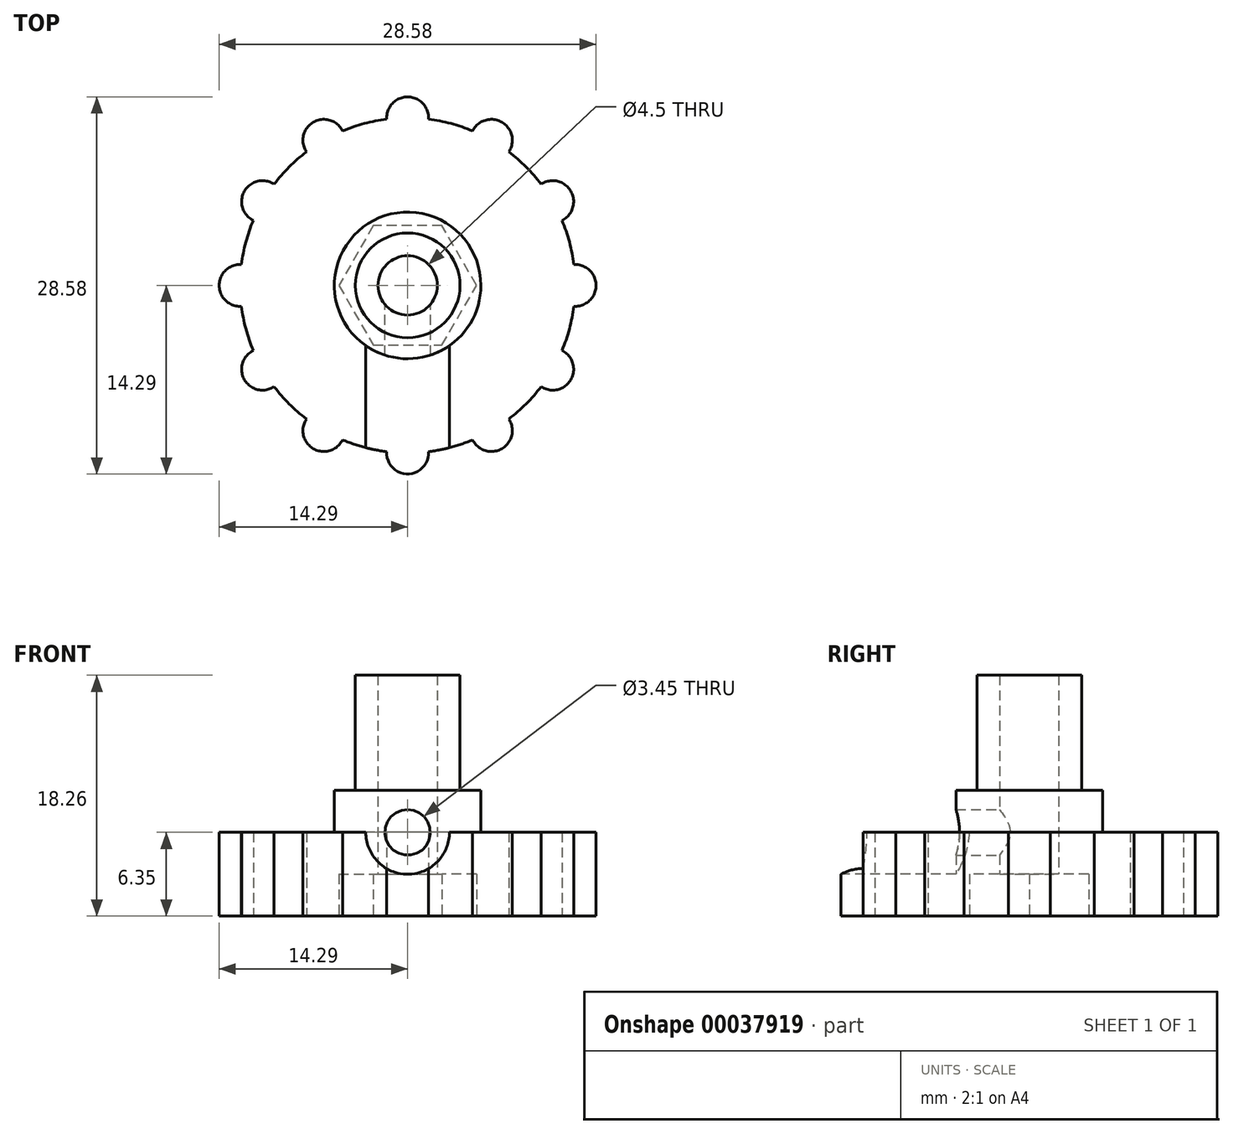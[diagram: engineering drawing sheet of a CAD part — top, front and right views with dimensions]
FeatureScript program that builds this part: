
annotation { "Feature Type Name" : "Feature", "Feature Type Description" : "" }
export const myFeature = defineFeature(function(context is Context, id is Id, definition is map)
    precondition{}
    {
        {
            var Q0;
            Q0=qCreatedBy(makeId("Top.planeOp"),FACE);
            var sketch = newSketch(context, id + "F0", { "sketchPlane" : qUnion([Q0])});
            skCircle(sketch, "E0", {"center": v(0, 0) * mm, "radius": 12.7 * mm});
            skSolve(sketch);
        }
        {
            var Q0;
            Q0 = qSketchRegion(id + "F0", true);
            extrude(context, id + "F1", {"entities" : qUnion([Q0]), "depth" : 6.35 * mm});
        }
        {
            var Q0;
            Q0=makeQuery(id+"F1.opExtrude","CAP_FACE",FACE,{"disambiguationData":[OSD([sQuery(id+"F0.wireOp",EDGE,"E0")])],"isStart":true});
            var sketch = newSketch(context, id + "F2", { "sketchPlane" : qUnion([Q0])});
            skCircle(sketch, "E1.cCircle", {"center": v(0, 0) * mm, "radius": 4.52 * mm, "construction": true});
            skLineSegment(sketch, "E1.0", {"start": v(-2.61, 4.52) * mm, "end": v(2.61, 4.52) * mm});
            skLineSegment(sketch, "E1.1", {"start": v(2.61, 4.52) * mm, "end": v(5.22, 0) * mm});
            skLineSegment(sketch, "E1.2", {"start": v(5.22, 0) * mm, "end": v(2.61, -4.52) * mm});
            skLineSegment(sketch, "E1.3", {"start": v(2.61, -4.52) * mm, "end": v(-2.61, -4.52) * mm});
            skLineSegment(sketch, "E1.4", {"start": v(-2.61, -4.52) * mm, "end": v(-5.22, 0) * mm});
            skLineSegment(sketch, "E1.5", {"start": v(-5.22, 0) * mm, "end": v(-2.61, 4.52) * mm});
            skPoint(sketch, "E1.0.midPoint", {"position": v(0, 4.52) * mm});
            skSolve(sketch);
        }
        {
            var Q0;
            Q0 = qSketchRegion(id + "F2", true);
            extrude(context, id + "F3", {"entities" : qUnion([Q0]), "operationType" : NewBodyOperationType.REMOVE, "oppositeDirection" : true, "depth" : 3.17 * mm});
        }
        {
            var Q0;
            Q0=makeQuery(id+"F1.opExtrude","CAP_FACE",FACE,{"disambiguationData":[OSD([sQuery(id+"F0.wireOp",EDGE,"E0")])],"isStart":false});
            var sketch = newSketch(context, id + "F4", { "sketchPlane" : qUnion([Q0])});
            skCircle(sketch, "E2", {"center": v(0, 0) * mm, "radius": 5.56 * mm});
            skSolve(sketch);
        }
        {
            var Q0;
            Q0 = qSketchRegion(id + "F4", true);
            extrude(context, id + "F5", {"entities" : qUnion([Q0]), "operationType" : NewBodyOperationType.ADD, "depth" : 3.17 * mm});
        }
        {
            var Q0;
            Q0=makeQuery(id+"F5.opExtrude","CAP_FACE",FACE,{"disambiguationData":[OSD([sQuery(id+"F4.wireOp",EDGE,"E2")])],"isStart":false});
            var sketch = newSketch(context, id + "F6", { "sketchPlane" : qUnion([Q0])});
            skCircle(sketch, "E3", {"center": v(0, 0) * mm, "radius": 3.97 * mm});
            skSolve(sketch);
        }
        {
            var Q0;
            Q0 = qSketchRegion(id + "F6", true);
            extrude(context, id + "F7", {"entities" : qUnion([Q0]), "operationType" : NewBodyOperationType.ADD, "depth" : 8.73 * mm});
        }
        {
            var Q0;
            Q0=makeQuery(id+"F3.boolean.opBoolean","COPY",FACE,{"derivedFrom":makeQuery(id+"F3.opExtrude","CAP_FACE",FACE,{"disambiguationData":[OSD([sQuery(id+"F2.wireOp",EDGE,"E1.0"),sQuery(id+"F2.wireOp",EDGE,"E1.1"),sQuery(id+"F2.wireOp",EDGE,"E1.2"),sQuery(id+"F2.wireOp",EDGE,"E1.3"),sQuery(id+"F2.wireOp",EDGE,"E1.4"),sQuery(id+"F2.wireOp",EDGE,"E1.5")])],"isStart":false})});
            var sketch = newSketch(context, id + "F8", { "sketchPlane" : qUnion([Q0])});
            skCircle(sketch, "E4", {"center": v(0, 0) * mm, "radius": 2.25 * mm});
            skSolve(sketch);
        }
        {
            var Q0;
            Q0 = qSketchRegion(id + "F8", true);
            var Q1;
            Q1=makeQuery(id+"F7.opExtrude","CAP_FACE",FACE,{"disambiguationData":[OSD([sQuery(id+"F6.wireOp",EDGE,"E3")])],"isStart":false});
            extrude(context, id + "F9", {"entities" : qUnion([Q0]), "operationType" : NewBodyOperationType.REMOVE, "endBound" : BoundingType.UP_TO_SURFACE, "oppositeDirection" : true, "endBoundEntityFace" : qUnion([Q1]), "depth" : 25.4 * mm});
        }
        {
            var Q0;
            Q0=makeQuery(id+"F1.opExtrude","CAP_FACE",FACE,{"disambiguationData":[OSD([sQuery(id+"F0.wireOp",EDGE,"E0")])],"isStart":true});
            var sketch = newSketch(context, id + "F10", { "sketchPlane" : qUnion([Q0])});
            skArc(sketch, "E5", {"start": v(1.58, 12.6) * mm, "mid": v(0, 14.29) * mm, "end": v(-1.58, 12.6) * mm});
            skArc(sketch, "E6", {"start": v(1.58, 12.6) * mm, "mid": v(0, 12.7) * mm, "end": v(-1.58, 12.6) * mm});
            skSolve(sketch);
        }
        {
            var Q0;
            Q0 = qSketchRegion(id + "F10", true);
            var Q1;
            Q1=makeQuery(id+"F1.opExtrude","CAP_FACE",FACE,{"disambiguationData":[OSD([sQuery(id+"F0.wireOp",EDGE,"E0")])],"isStart":false});
            extrude(context, id + "F11", {"entities" : qUnion([Q0]), "operationType" : NewBodyOperationType.ADD, "endBound" : BoundingType.UP_TO_SURFACE, "oppositeDirection" : true, "endBoundEntityFace" : qUnion([Q1]), "depth" : 25.4 * mm});
        }
        {
            var Q0;
            Q0=makeQuery(id+"F11.opExtrude","SWEPT_FACE",FACE,{"disambiguationData":[OSD([sQuery(id+"F10.wireOp",EDGE,"E5")])]});
            var Q1;
            Q1=makeQuery(id+"F1.opExtrude","SWEPT_FACE",FACE,{"disambiguationData":[OSD([sQuery(id+"F0.wireOp",EDGE,"E0")])]});
            circularPattern(context, id + "F12", {"operationType" : NewBodyOperationType.ADD, "faces" : qUnion([Q0]), "axis" : qUnion([Q1]), "angle" : 30 * degree, "instanceCount" : 12, "patternType" : PatternType.FACE});
        }
        {
            var Q0;
            Q0=qCreatedBy(makeId("Front.planeOp"),FACE);
            var sketch = newSketch(context, id + "F13", { "sketchPlane" : qUnion([Q0])});
            skLineSegment(sketch, "E7", {"start": v(0, 3.18) * mm, "end": v(0, 9.53) * mm});
            skCircle(sketch, "E8", {"center": v(0, 6.35) * mm, "radius": 1.73 * mm});
            skSolve(sketch);
        }
        {
            var Q0;
            Q0 = qSketchRegion(id + "F13", true);
            var Q1;
            Q1=makeQuery(id+"F5.opExtrude","SWEPT_FACE",FACE,{"disambiguationData":[OSD([sQuery(id+"F4.wireOp",EDGE,"E2")])]});
            extrude(context, id + "F14", {"entities" : qUnion([Q0]), "operationType" : NewBodyOperationType.REMOVE, "endBound" : BoundingType.UP_TO_SURFACE, "endBoundEntityFace" : qUnion([Q1]), "depth" : 25.4 * mm});
        }
        {
            var Q0;
            Q0=qCreatedBy(makeId("Front.planeOp"),FACE);
            cPlane(context, id + "F15", {"entities" : qUnion([Q0]), "cplaneType" : CPlaneType.OFFSET, "offset" : 14.29 * mm, "width" : 152.4 * mm, "height" : 152.4 * mm});
        }
        {
            var Q0;
            Q0=qCreatedBy(id+"F15.planeOp",FACE);
            var sketch = newSketch(context, id + "F16", { "sketchPlane" : qUnion([Q0])});
            skArc(sketch, "E9", {"start": v(3.17, 6.35) * mm, "mid": v(0, 9.53) * mm, "end": v(-3.18, 6.35) * mm, "construction": true});
            skArc(sketch, "E10", {"start": v(-3.18, 6.35) * mm, "mid": v(0, 3.17) * mm, "end": v(3.17, 6.35) * mm});
            skLineSegment(sketch, "E11", {"start": v(-3.18, 6.35) * mm, "end": v(3.17, 6.35) * mm});
            skSolve(sketch);
        }
        {
            var Q0;
            Q0 = qSketchRegion(id + "F16", true);
            var Q1;
            Q1=makeQuery(id+"F5.opExtrude","SWEPT_FACE",FACE,{"disambiguationData":[OSD([sQuery(id+"F4.wireOp",EDGE,"E2")])]});
            extrude(context, id + "F17", {"entities" : qUnion([Q0]), "operationType" : NewBodyOperationType.REMOVE, "endBound" : BoundingType.UP_TO_SURFACE, "oppositeDirection" : true, "endBoundEntityFace" : qUnion([Q1]), "depth" : 25.4 * mm});
        }
    });
